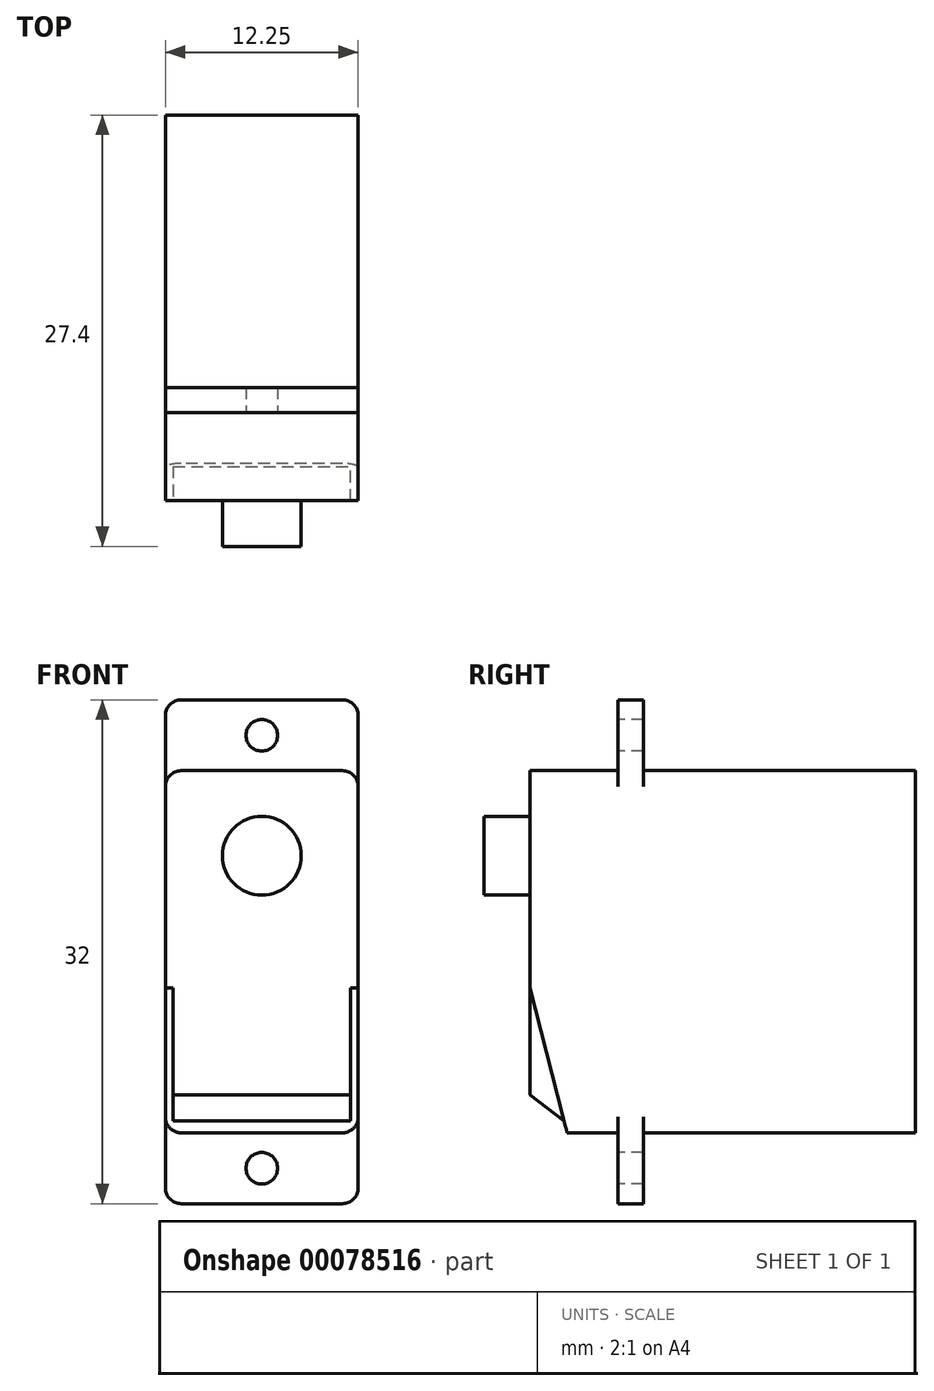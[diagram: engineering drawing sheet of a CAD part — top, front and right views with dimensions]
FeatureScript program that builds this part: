
annotation { "Feature Type Name" : "Feature", "Feature Type Description" : "" }
export const myFeature = defineFeature(function(context is Context, id is Id, definition is map)
    precondition{}
    {
        {
            var Q0;
            Q0=qCreatedBy(makeId("Right.planeOp"),FACE);
            var sketch = newSketch(context, id + "F0", { "sketchPlane" : qUnion([Q0])});
            skLineSegment(sketch, "E0", {"start": v(12.25, -11.5) * mm, "end": v(12.25, 11.5) * mm});
            skLineSegment(sketch, "E1", {"start": v(-12.25, 11.5) * mm, "end": v(-12.25, -2.3) * mm});
            skLineSegment(sketch, "E2", {"start": v(-12.25, -2.3) * mm, "end": v(-9.88, -11.5) * mm});
            skLineSegment(sketch, "E3", {"start": v(-12.25, 11.5) * mm, "end": v(-6.65, 11.5) * mm});
            skLineSegment(sketch, "E4", {"start": v(-6.65, 11.5) * mm, "end": v(-6.65, 16) * mm});
            skLineSegment(sketch, "E5", {"start": v(-6.65, 16) * mm, "end": v(-5.05, 16) * mm});
            skLineSegment(sketch, "E6", {"start": v(-5.05, 16) * mm, "end": v(-5.05, 11.5) * mm});
            skLineSegment(sketch, "E7", {"start": v(-5.05, 11.5) * mm, "end": v(12.25, 11.5) * mm});
            skLineSegment(sketch, "E8", {"start": v(-9.88, -11.5) * mm, "end": v(-6.65, -11.5) * mm});
            skLineSegment(sketch, "E9", {"start": v(-6.65, -11.5) * mm, "end": v(-6.65, -16) * mm});
            skLineSegment(sketch, "E10", {"start": v(-6.65, -16) * mm, "end": v(-5.05, -16) * mm});
            skLineSegment(sketch, "E11", {"start": v(-5.05, -16) * mm, "end": v(-5.05, -11.5) * mm});
            skLineSegment(sketch, "E12", {"start": v(-5.05, -11.5) * mm, "end": v(12.25, -11.5) * mm});
            skLineSegment(sketch, "E13", {"start": v(0, 11.5) * mm, "end": v(0, -11.5) * mm, "construction": true});
            skLineSegment(sketch, "E14", {"start": v(-12.25, 0) * mm, "end": v(12.25, 0) * mm, "construction": true});
            skPoint(sketch, "E15", {"position": v(0, 0) * mm});
            skSolve(sketch);
        }
        {
            var Q0;
            Q0 = qSketchRegion(id + "F0", true);
            extrude(context, id + "F1", {"entities" : qUnion([Q0]), "depth" : 12.25 * mm});
        }
        {
            var Q0;
            Q0=makeQuery(id+"F1.opExtrude","CAP_FACE",FACE,{"disambiguationData":[OSD([sQuery(id+"F0.wireOp",EDGE,"E0"),sQuery(id+"F0.wireOp",EDGE,"E1"),sQuery(id+"F0.wireOp",EDGE,"E2"),sQuery(id+"F0.wireOp",EDGE,"E3"),sQuery(id+"F0.wireOp",EDGE,"E4"),sQuery(id+"F0.wireOp",EDGE,"E5"),sQuery(id+"F0.wireOp",EDGE,"E6"),sQuery(id+"F0.wireOp",EDGE,"E7"),sQuery(id+"F0.wireOp",EDGE,"E8"),sQuery(id+"F0.wireOp",EDGE,"E9"),sQuery(id+"F0.wireOp",EDGE,"E10"),sQuery(id+"F0.wireOp",EDGE,"E11"),sQuery(id+"F0.wireOp",EDGE,"E12")])],"isStart":false});
            cPlane(context, id + "F2", {"entities" : qUnion([Q0]), "cplaneType" : CPlaneType.OFFSET, "offset" : .5 * mm, "oppositeDirection" : true, "width" : 150 * mm, "height" : 150 * mm});
        }
        {
            var Q0;
            Q0=qCreatedBy(makeId("Right.planeOp"),FACE);
            cPlane(context, id + "F3", {"entities" : qUnion([Q0]), "cplaneType" : CPlaneType.OFFSET, "offset" : .5 * mm, "width" : 150 * mm, "height" : 150 * mm});
        }
        {
            var Q0;
            Q0=qCreatedBy(id+"F2.planeOp",FACE);
            var sketch = newSketch(context, id + "F4", { "sketchPlane" : qUnion([Q0])});
            skPoint(sketch, "E16.0", {"position": v(-12.25, -2.3) * mm});
            skLineSegment(sketch, "E17", {"start": v(-12.25, -2.3) * mm, "end": v(-12.25, -9.1) * mm});
            skLineSegment(sketch, "E18.0", {"start": v(-12.25, -2.3) * mm, "end": v(-9.88, -11.5) * mm});
            skLineSegment(sketch, "E19", {"start": v(-12.25, -9.1) * mm, "end": v(-10.07, -10.75) * mm});
            skSolve(sketch);
        }
        {
            var Q0;
            Q0 = qSketchRegion(id + "F4", true);
            var Q1;
            Q1=qCreatedBy(id+"F3.planeOp",FACE);
            extrude(context, id + "F5", {"entities" : qUnion([Q0]), "operationType" : NewBodyOperationType.ADD, "endBound" : BoundingType.UP_TO_SURFACE, "oppositeDirection" : true, "endBoundEntityFace" : qUnion([Q1]), "depth" : 25 * mm});
        }
        {
            var Q0;
            Q0=makeQuery(id+"F5.boolean.opBoolean","MERGE",FACE,{"derivedFrom":[makeQuery(id+"F1.opExtrude","SWEPT_FACE",FACE,{"disambiguationData":[OSD([sQuery(id+"F0.wireOp",EDGE,"E1")])]}),makeQuery(id+"F5.opExtrude","SWEPT_FACE",FACE,{"disambiguationData":[OSD([sQuery(id+"F4.wireOp",EDGE,"E17")])]})]});
            var sketch = newSketch(context, id + "F6", { "sketchPlane" : qUnion([Q0])});
            skCircle(sketch, "E20", {"center": v(6.13, 6.1) * mm, "radius": 2.5 * mm});
            skLineSegment(sketch, "E21.0", {"start": v(12.25, 16) * mm, "end": v(0, 16) * mm});
            skPoint(sketch, "E22", {"position": v(6.12, 16) * mm});
            skSolve(sketch);
        }
        {
            var Q0;
            Q0 = qSketchRegion(id + "F6", true);
            extrude(context, id + "F7", {"entities" : qUnion([Q0]), "operationType" : NewBodyOperationType.ADD, "depth" : 2.9 * mm});
        }
        {
            var Q0;
            Q0=makeQuery(id+"F1.opExtrude","SWEPT_FACE",FACE,{"disambiguationData":[OSD([sQuery(id+"F0.wireOp",EDGE,"E4")])]});
            var sketch = newSketch(context, id + "F8", { "sketchPlane" : qUnion([Q0])});
            skPoint(sketch, "E23.0", {"position": v(6.12, 16) * mm});
            skCircle(sketch, "E24", {"center": v(6.12, 13.75) * mm, "radius": 1 * mm});
            skCircle(sketch, "E25", {"center": v(6.12, -13.75) * mm, "radius": 1 * mm});
            skPoint(sketch, "E26", {"position": v(12.25, 13.75) * mm});
            skLineSegment(sketch, "E27.0", {"start": v(12.25, -11.5) * mm, "end": v(12.25, -16) * mm});
            skPoint(sketch, "E28", {"position": v(12.25, -13.75) * mm});
            skSolve(sketch);
        }
        {
            var Q0;
            Q0 = qSketchRegion(id + "F8", true);
            extrude(context, id + "F9", {"entities" : qUnion([Q0]), "operationType" : NewBodyOperationType.REMOVE, "endBound" : BoundingType.THROUGH_ALL, "oppositeDirection" : true, "depth" : 25 * mm});
        }
        {
            var Q0;
            Q0=makeQuery(id+"F1.opExtrude","CAP_EDGE",EDGE,{"disambiguationData":[OSD([sQuery(id+"F0.wireOp",EDGE,"E7")])],"isStart":false});
            var Q1;
            Q1=makeQuery(id+"F1.opExtrude","CAP_EDGE",EDGE,{"disambiguationData":[OSD([sQuery(id+"F0.wireOp",EDGE,"E3")])],"isStart":false});
            var Q2;
            Q2=makeQuery(id+"F1.opExtrude","CAP_EDGE",EDGE,{"disambiguationData":[OSD([sQuery(id+"F0.wireOp",EDGE,"E12")])],"isStart":false});
            var Q3;
            Q3=makeQuery(id+"F1.opExtrude","CAP_EDGE",EDGE,{"disambiguationData":[OSD([sQuery(id+"F0.wireOp",EDGE,"E8")])],"isStart":false});
            var Q4;
            Q4=makeQuery(id+"F1.opExtrude","CAP_EDGE",EDGE,{"disambiguationData":[OSD([sQuery(id+"F0.wireOp",EDGE,"E8")])],"isStart":true});
            var Q5;
            Q5=makeQuery(id+"F1.opExtrude","CAP_EDGE",EDGE,{"disambiguationData":[OSD([sQuery(id+"F0.wireOp",EDGE,"E12")])],"isStart":true});
            var Q6;
            Q6=makeQuery(id+"F1.opExtrude","CAP_EDGE",EDGE,{"disambiguationData":[OSD([sQuery(id+"F0.wireOp",EDGE,"E7")])],"isStart":true});
            var Q7;
            Q7=makeQuery(id+"F1.opExtrude","CAP_EDGE",EDGE,{"disambiguationData":[OSD([sQuery(id+"F0.wireOp",EDGE,"E3")])],"isStart":true});
            var Q8;
            Q8=makeQuery(id+"F1.opExtrude","CAP_EDGE",EDGE,{"disambiguationData":[OSD([sQuery(id+"F0.wireOp",EDGE,"E5")])],"isStart":true});
            var Q9;
            Q9=makeQuery(id+"F1.opExtrude","CAP_EDGE",EDGE,{"disambiguationData":[OSD([sQuery(id+"F0.wireOp",EDGE,"E5")])],"isStart":false});
            var Q10;
            Q10=makeQuery(id+"F1.opExtrude","CAP_EDGE",EDGE,{"disambiguationData":[OSD([sQuery(id+"F0.wireOp",EDGE,"E10")])],"isStart":true});
            var Q11;
            Q11=makeQuery(id+"F1.opExtrude","CAP_EDGE",EDGE,{"disambiguationData":[OSD([sQuery(id+"F0.wireOp",EDGE,"E10")])],"isStart":false});
            fillet(context, id + "F10", {"entities" : qUnion([Q0, Q1, Q2, Q3, Q4, Q5, Q6, Q7, Q8, Q9, Q10, Q11]), "radius" : 1 * mm, "tangentPropagation" : true, "allowEdgeOverflow" : false});
        }
    });
